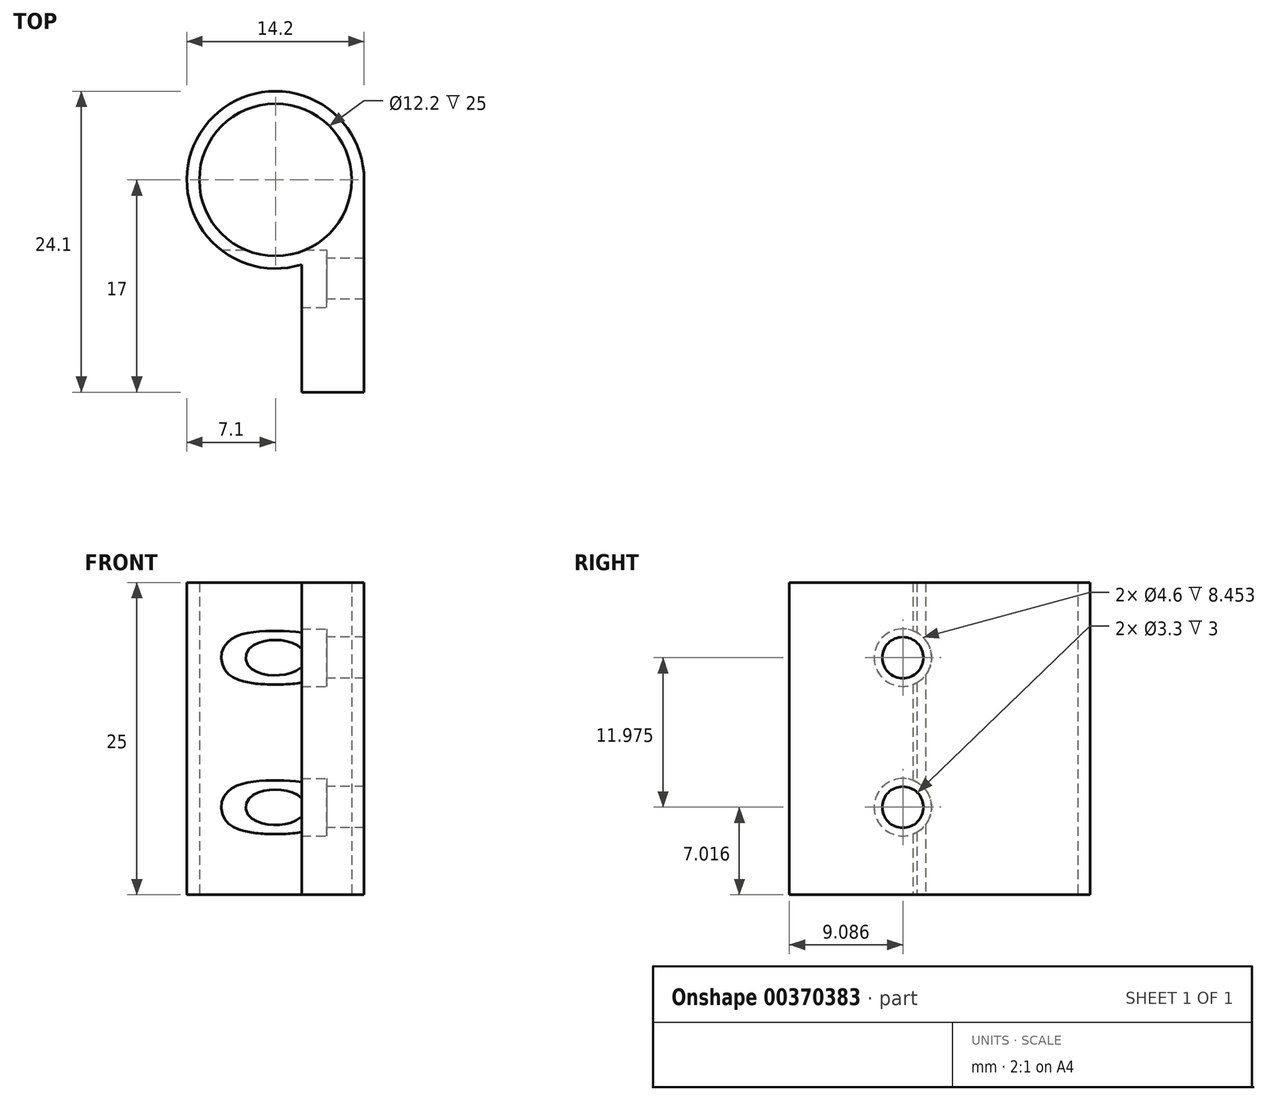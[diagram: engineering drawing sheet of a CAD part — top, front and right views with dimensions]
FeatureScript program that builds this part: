
annotation { "Feature Type Name" : "Feature", "Feature Type Description" : "" }
export const myFeature = defineFeature(function(context is Context, id is Id, definition is map)
    precondition{}
    {
        {
            var Q0;
            Q0=qCreatedBy(makeId("Top.planeOp"),FACE);
            var sketch = newSketch(context, id + "F0", { "sketchPlane" : qUnion([Q0])});
            skLineSegment(sketch, "E0.right", {"start": v(0, 0) * mm, "end": v(0, 0) * mm});
            skCircle(sketch, "E1", {"center": v(0, 0) * mm, "radius": 6.1 * mm});
            skCircle(sketch, "E2", {"center": v(0, 0) * mm, "radius": 7.1 * mm});
            skLineSegment(sketch, "E3.MirrorCS", {"start": v(7.1, 0) * mm, "end": v(7.1, -17) * mm});
            skLineSegment(sketch, "E4.MirrorCS", {"start": v(2.1, -17) * mm, "end": v(2.1, -6.78) * mm});
            skLineSegment(sketch, "E5.MirrorCS", {"start": v(7.1, -17) * mm, "end": v(2.1, -17) * mm});
            skLineSegment(sketch, "E6", {"start": v(-8.56, 0) * mm, "end": v(8.94, 0) * mm, "construction": true});
            skPoint(sketch, "E7", {"position": v(7.1, 0) * mm});
            skSolve(sketch);
        }
        {
            var Q0;
            Q0 = qSketchRegion(id + "F0", true);
            extrude(context, id + "F1", {"entities" : qUnion([Q0]), "depth" : 25 * mm});
        }
        {
            var Q0;
            Q0=makeQuery(id+"F1.opExtrude","SWEPT_FACE",FACE,{"disambiguationData":[OSD([sQuery(id+"F0.wireOp",EDGE,"E4.MirrorCS")])]});
            var sketch = newSketch(context, id + "F2", { "sketchPlane" : qUnion([Q0])});
            skLineSegment(sketch, "E8", {"start": v(7.91, 25) * mm, "end": v(7.91, 0) * mm, "construction": true});
            skLineSegment(sketch, "E9", {"start": v(17, 7.02) * mm, "end": v(6.78, 7.02) * mm, "construction": true});
            skLineSegment(sketch, "E10", {"start": v(17, 19) * mm, "end": v(6.78, 19) * mm, "construction": true});
            skLineSegment(sketch, "E11", {"start": v(-7.09, 25) * mm, "end": v(-7.09, 12.7) * mm, "construction": true});
            skPoint(sketch, "E12", {"position": v(7.91, 19) * mm});
            skPoint(sketch, "E13", {"position": v(7.91, 7.02) * mm});
            skCircle(sketch, "E14", {"center": v(7.91, 19) * mm, "radius": 2.3 * mm});
            skCircle(sketch, "E15", {"center": v(7.91, 7.02) * mm, "radius": 2.3 * mm});
            skSolve(sketch);
        }
        {
            var Q0;
            {var subQ0=sQuery(id+"F2.wireOp",EDGE,"E14");var subQ1=makeQuery(id+"F1.opExtrude","SWEPT_EDGE",EDGE,{"disambiguationData":[OSD([sQuery(id+"F0.wireOp",EDGE,"E2"),sQuery(id+"F0.wireOp",EDGE,"E4.MirrorCS")])]});var subQ2=makeQuery(id+"F2.imprint","INTERSECT",VERTEX,{"disambiguationData":[OD(0.0)],"derivedFrom":[subQ1,subQ0]});Q0=makeQuery(id+"F2.imprint","IMPRINT",FACE,{"disambiguationData":[TD([[makeQuery(id+"F2.imprint","IMPRINT",EDGE,{"disambiguationData":[TD([[subQ2,1.0]])],"derivedFrom":subQ0}),1.0]])]});}
            var Q1;
            Q1 = qSketchRegion(id + "F2", true);
            extrude(context, id + "F3", {"entities" : qUnion([Q0, Q1]), "operationType" : NewBodyOperationType.REMOVE, "depth" : 25 * mm});
        }
        {
            var Q0;
            Q0 = qSketchRegion(id + "F2", true);
            extrude(context, id + "F4", {"entities" : qUnion([Q0]), "operationType" : NewBodyOperationType.REMOVE, "oppositeDirection" : true, "depth" : 2 * mm});
        }
        {
            var Q0;
            Q0=sQuery(id+"F2.wireOp",VERTEX,"E13");
            var Q1;
            Q1=sQuery(id+"F2.wireOp",VERTEX,"E12");
            var Q2;
            Q2=makeQuery(id+"F1.opExtrude","SWEPT_BODY",BODY,{"disambiguationData":[OSD([sQuery(id+"F0.wireOp",EDGE,"E1"),sQuery(id+"F0.wireOp",EDGE,"E2"),sQuery(id+"F0.wireOp",EDGE,"E3.MirrorCS"),sQuery(id+"F0.wireOp",EDGE,"E4.MirrorCS"),sQuery(id+"F0.wireOp",EDGE,"E5.MirrorCS")])]});
            hole(context, id + "F5", {"style" : HoleStyle.SIMPLE, "endStyle" : HoleEndStyle.THROUGH, "standardTappedOrClearance" : lookupTablePath({ "standard" : "ISO", "fit" : "Normal", "size" : "M3", "type" : "Clearance" }), "standardBlindInLast" : lookupTablePath({ "fit" : "Standard", "standard" : "ISO", "size" : "M3", "type" : "Clearance" }), "holeDiameter" : 3.3 * mm, "tappedDepth" : 12 * mm, "tapClearance" : 3, "locations" : qUnion([Q0, Q1]), "scope" : qUnion([Q2])});
        }
    });
